# Revit family: Mounted Bahama Classic w Center Rail
name_source: partatom
category: Generic Models
revit_build: Autodesk Revit 2017 (Build: 20160225_1515(x64)
units: mm (PartAtom-declared; Revit-internal decimal feet)

## family parameters
Always vertical = Yes
Can host rebar = No
Cut with Voids When Loaded = No
Part Type = Normal
Room Calculation Point = No
Round Connector Dimension = Use Diameter
Shared = No
Work Plane-Based = No

## types (1)
- Mounted Bahama Classic w Center Rail
    1 Vertical Mullion = No
    2 Vertical Mullions = Yes
    3 Vertical Mullions = No
    Attachment Height = 7' - 8 9/32"
    Bottom Rail = 0' - 3 1/4"
    Finish Color = Default
    Manufacturer = New Horizon Shutters
    Mid Rail = 0' - 2 1/4"
    Mid Rail Height = 3' - 0"
    Model = Bahama Classic With Center Rail
    Shutter Angle = 20.00°
    Shutter Attachment Width = 6' - 0"
    Shutter Height = 6' - 0"
    Shutter Width = 6' - 0"
    Top Rail = 0' - 3 1/4"
    Type Comments = **** All shutter dimensions and configurations to be approved by NHSI ****
    URL = www.newhorizonshutters.com

## geometry (parser evidence)
native form markers: Sweep x19
no freeform markers — native parametric forms only
